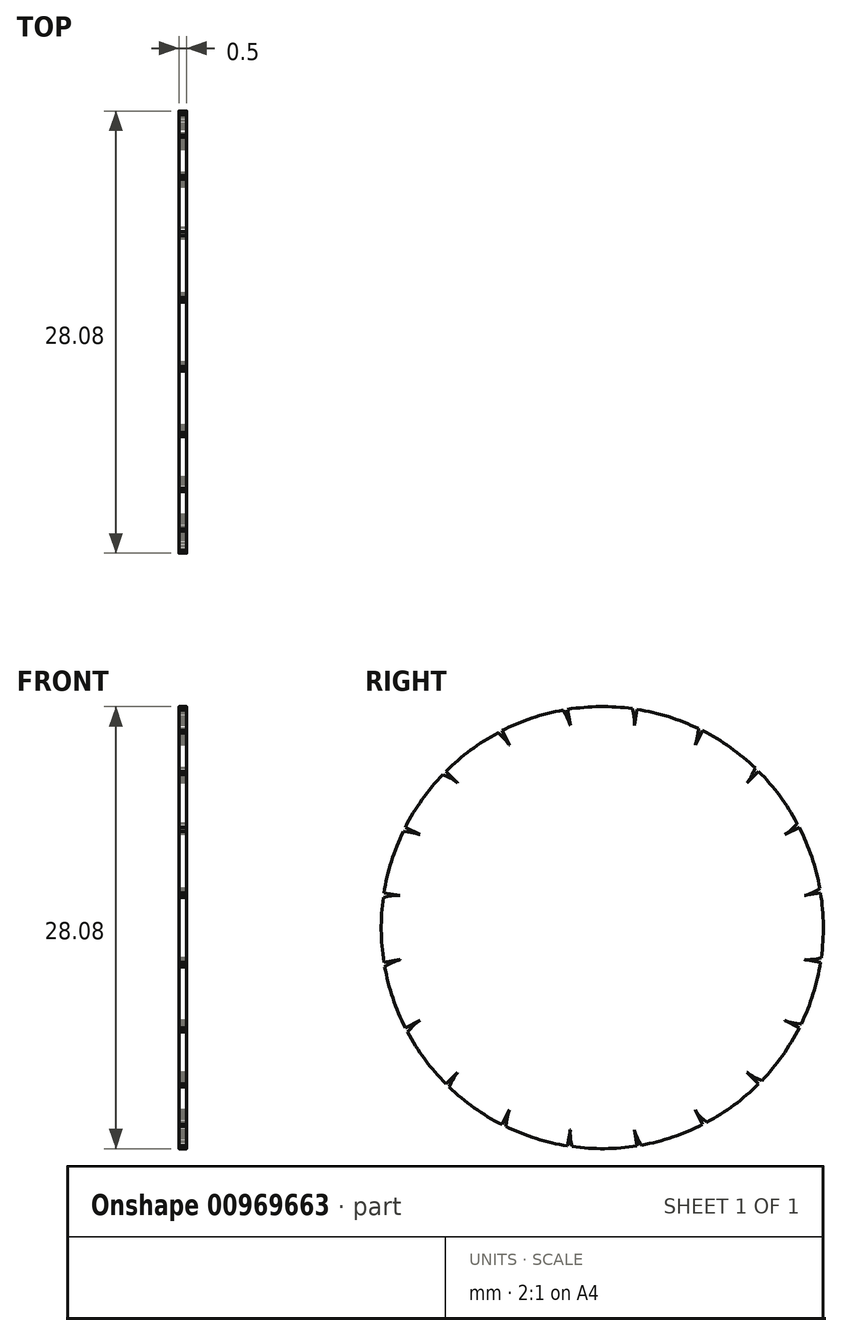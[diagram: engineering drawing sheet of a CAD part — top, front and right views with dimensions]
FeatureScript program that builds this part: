
annotation { "Feature Type Name" : "Feature", "Feature Type Description" : "" }
export const myFeature = defineFeature(function(context is Context, id is Id, definition is map)
    precondition{}
    {
        {
            assignVariable(context, id + "F0", {"name" : "GearThickness", "anyValue" : .5});
        }
        {
            var Q0;
            Q0=qCreatedBy(makeId("Right.planeOp"),FACE);
            var sketch = newSketch(context, id + "F1", { "sketchPlane" : qUnion([Q0])});
            skCircle(sketch, "E0", {"center": v(0, 0) * mm, "radius": 14.04 * mm});
            skCircle(sketch, "E1", {"center": v(0, 0) * mm, "radius": 13 * mm, "construction": true});
            skCircle(sketch, "E2", {"center": v(0, 0) * mm, "radius": 15.88 * mm, "construction": true});
            skCircle(sketch, "E3", {"center": v(0, 0) * mm, "radius": 17.46 * mm});
            skLineSegment(sketch, "E4", {"start": v(0, 0) * mm, "end": v(-13, 0) * mm, "construction": true});
            skLineSegment(sketch, "E5.1.0", {"start": v(0, 0) * mm, "end": v(-12.99, 0.65) * mm, "construction": true});
            skLineSegment(sketch, "E5.2.0", {"start": v(0, 0) * mm, "end": v(-12.94, 1.3) * mm, "construction": true});
            skLineSegment(sketch, "E5.3.0", {"start": v(0, 0) * mm, "end": v(-12.86, 1.94) * mm, "construction": true});
            skLineSegment(sketch, "E5.4.0", {"start": v(0, 0) * mm, "end": v(-12.74, 2.58) * mm, "construction": true});
            skLineSegment(sketch, "E5.5.0", {"start": v(0, 0) * mm, "end": v(-12.6, 3.22) * mm, "construction": true});
            skLineSegment(sketch, "E5.6.0", {"start": v(0, 0) * mm, "end": v(-12.42, 3.84) * mm, "construction": true});
            skLineSegment(sketch, "E5.7.0", {"start": v(0, 0) * mm, "end": v(-12.22, 4.46) * mm, "construction": true});
            skLineSegment(sketch, "E5.8.0", {"start": v(0, 0) * mm, "end": v(-11.98, 5.06) * mm, "construction": true});
            skLineSegment(sketch, "E5.9.0", {"start": v(0, 0) * mm, "end": v(-11.7, 5.66) * mm, "construction": true});
            skLineSegment(sketch, "E5.10.0", {"start": v(0, 0) * mm, "end": v(-11.41, 6.23) * mm, "construction": true});
            skLineSegment(sketch, "E5.11.0", {"start": v(0, 0) * mm, "end": v(-11.09, 6.8) * mm, "construction": true});
            skLineSegment(sketch, "E5.12.0", {"start": v(0, 0) * mm, "end": v(-10.73, 7.34) * mm, "construction": true});
            skLineSegment(sketch, "E5.13.0", {"start": v(0, 0) * mm, "end": v(-10.35, 7.87) * mm, "construction": true});
            skLineSegment(sketch, "E5.14.0", {"start": v(0, 0) * mm, "end": v(-9.95, 8.38) * mm, "construction": true});
            skLineSegment(sketch, "E5.anchor2", {"start": v(0, 0) * mm, "end": v(-9.95, 8.38) * mm, "construction": true});
            skLineSegment(sketch, "E6", {"start": v(-12.99, 0.65) * mm, "end": v(-13.02, 0) * mm, "construction": true});
            skLineSegment(sketch, "E7", {"start": v(-12.94, 1.3) * mm, "end": v(-13.07, 0) * mm, "construction": true});
            skLineSegment(sketch, "E8", {"start": v(-12.86, 1.94) * mm, "end": v(-13.15, 0.01) * mm, "construction": true});
            skLineSegment(sketch, "E9", {"start": v(-12.6, 3.22) * mm, "end": v(-13.4, 0.07) * mm, "construction": true});
            skLineSegment(sketch, "E10", {"start": v(-12.42, 3.84) * mm, "end": v(-13.58, 0.12) * mm, "construction": true});
            skLineSegment(sketch, "E11", {"start": v(-12.22, 4.46) * mm, "end": v(-13.78, 0.18) * mm, "construction": true});
            skLineSegment(sketch, "E12", {"start": v(-11.98, 5.06) * mm, "end": v(-14, 0.27) * mm, "construction": true});
            skLineSegment(sketch, "E13", {"start": v(-11.7, 5.66) * mm, "end": v(-14.25, 0.39) * mm, "construction": true});
            skLineSegment(sketch, "E14", {"start": v(-11.41, 6.23) * mm, "end": v(-14.53, 0.53) * mm, "construction": true});
            skLineSegment(sketch, "E15", {"start": v(-11.09, 6.8) * mm, "end": v(-14.82, 0.7) * mm, "construction": true});
            skLineSegment(sketch, "E16", {"start": v(-12.74, 2.58) * mm, "end": v(-13.26, 0.03) * mm, "construction": true});
            skLineSegment(sketch, "E17", {"start": v(-10.73, 7.34) * mm, "end": v(-15.14, 0.9) * mm, "construction": true});
            skLineSegment(sketch, "E18", {"start": v(-10.35, 7.87) * mm, "end": v(-15.47, 1.14) * mm, "construction": true});
            skLineSegment(sketch, "E19", {"start": v(-9.95, 8.38) * mm, "end": v(-15.81, 1.42) * mm, "construction": true});
            skLineSegment(sketch, "E20", {"start": v(0, 0) * mm, "end": v(-12.96, 1.02) * mm, "construction": true});
            skLineSegment(sketch, "E21", {"start": v(-13, 0) * mm, "end": v(-14.04, 0) * mm});
            skLineSegment(sketch, "E22.MirrorCS", {"start": v(-12.84, 2.03) * mm, "end": v(-13.87, 2.2) * mm});
            skLineSegment(sketch, "E23", {"start": v(-13, 0) * mm, "end": v(-13.02, 0) * mm});
            skLineSegment(sketch, "E24", {"start": v(-13.02, 0) * mm, "end": v(-13.07, 0) * mm});
            skLineSegment(sketch, "E25", {"start": v(-13.07, 0) * mm, "end": v(-13.15, 0.01) * mm});
            skLineSegment(sketch, "E26", {"start": v(-13.15, 0.01) * mm, "end": v(-13.26, 0.03) * mm});
            skLineSegment(sketch, "E27", {"start": v(-13.26, 0.03) * mm, "end": v(-13.4, 0.07) * mm});
            skLineSegment(sketch, "E28", {"start": v(-13.4, 0.07) * mm, "end": v(-13.58, 0.12) * mm});
            skLineSegment(sketch, "E29", {"start": v(-13.58, 0.12) * mm, "end": v(-13.78, 0.18) * mm});
            skLineSegment(sketch, "E30", {"start": v(-13.78, 0.18) * mm, "end": v(-14, 0.27) * mm});
            skLineSegment(sketch, "E31", {"start": v(-14, 0.27) * mm, "end": v(-14.25, 0.39) * mm});
            skLineSegment(sketch, "E32", {"start": v(-14.25, 0.39) * mm, "end": v(-14.53, 0.53) * mm});
            skLineSegment(sketch, "E33", {"start": v(-14.53, 0.53) * mm, "end": v(-14.82, 0.7) * mm});
            skLineSegment(sketch, "E34", {"start": v(-14.82, 0.7) * mm, "end": v(-15.14, 0.9) * mm});
            skLineSegment(sketch, "E35", {"start": v(-15.14, 0.9) * mm, "end": v(-15.47, 1.14) * mm});
            skLineSegment(sketch, "E36", {"start": v(-15.47, 1.14) * mm, "end": v(-15.81, 1.42) * mm});
            skLineSegment(sketch, "E37.MirrorCS", {"start": v(-12.84, 2.03) * mm, "end": v(-12.86, 2.04) * mm});
            skLineSegment(sketch, "E38.MirrorCS", {"start": v(-12.86, 2.04) * mm, "end": v(-12.9, 2.04) * mm});
            skLineSegment(sketch, "E39.MirrorCS", {"start": v(-12.9, 2.04) * mm, "end": v(-12.99, 2.04) * mm});
            skLineSegment(sketch, "E40.MirrorCS", {"start": v(-12.99, 2.04) * mm, "end": v(-13.1, 2.04) * mm});
            skLineSegment(sketch, "E41.MirrorCS", {"start": v(-13.25, 2.03) * mm, "end": v(-13.43, 2) * mm});
            skLineSegment(sketch, "E42.MirrorCS", {"start": v(-13.43, 2) * mm, "end": v(-13.64, 1.97) * mm});
            skLineSegment(sketch, "E43.MirrorCS", {"start": v(-13.64, 1.97) * mm, "end": v(-13.87, 1.92) * mm});
            skLineSegment(sketch, "E44.MirrorCS", {"start": v(-13.87, 1.92) * mm, "end": v(-14.14, 1.85) * mm});
            skLineSegment(sketch, "E45.MirrorCS", {"start": v(-14.43, 1.75) * mm, "end": v(-14.75, 1.63) * mm});
            skLineSegment(sketch, "E46.MirrorCS", {"start": v(-14.14, 1.85) * mm, "end": v(-14.43, 1.75) * mm});
            skLineSegment(sketch, "E47.MirrorCS", {"start": v(-14.75, 1.63) * mm, "end": v(-15.1, 1.48) * mm});
            skLineSegment(sketch, "E48.MirrorCS", {"start": v(-15.1, 1.48) * mm, "end": v(-15.46, 1.3) * mm});
            skLineSegment(sketch, "E49.MirrorCS", {"start": v(-15.46, 1.3) * mm, "end": v(-15.84, 1.08) * mm});
            skLineSegment(sketch, "E50.MirrorCS", {"start": v(-13.1, 2.04) * mm, "end": v(-13.25, 2.03) * mm});
            skLineSegment(sketch, "E51.1.0", {"start": v(-12.37, -4.02) * mm, "end": v(-13.35, -4.34) * mm});
            skLineSegment(sketch, "E51.1.1", {"start": v(-14.53, -3.01) * mm, "end": v(-14.81, -3.26) * mm});
            skLineSegment(sketch, "E51.1.2", {"start": v(-12.84, -2.03) * mm, "end": v(-13.87, -2.2) * mm});
            skLineSegment(sketch, "E51.1.3", {"start": v(-14.27, -2.8) * mm, "end": v(-14.53, -3.01) * mm});
            skLineSegment(sketch, "E51.1.4", {"start": v(-13.98, -3.99) * mm, "end": v(-14.32, -3.92) * mm});
            skLineSegment(sketch, "E51.1.5", {"start": v(-14.32, -3.92) * mm, "end": v(-14.68, -3.82) * mm});
            skLineSegment(sketch, "E51.1.6", {"start": v(-14.02, -2.61) * mm, "end": v(-14.27, -2.8) * mm});
            skLineSegment(sketch, "E51.1.7", {"start": v(-15.1, -3.55) * mm, "end": v(-15.4, -3.87) * mm});
            skLineSegment(sketch, "E51.1.8", {"start": v(-13.79, -2.46) * mm, "end": v(-14.02, -2.61) * mm});
            skLineSegment(sketch, "E51.1.9", {"start": v(-15.06, -3.7) * mm, "end": v(-15.47, -3.54) * mm});
            skLineSegment(sketch, "E51.1.10", {"start": v(-14.81, -3.26) * mm, "end": v(-15.1, -3.55) * mm});
            skLineSegment(sketch, "E51.1.11", {"start": v(-13.68, -4.04) * mm, "end": v(-13.98, -3.99) * mm});
            skLineSegment(sketch, "E51.1.12", {"start": v(-14.68, -3.82) * mm, "end": v(-15.06, -3.7) * mm});
            skLineSegment(sketch, "E51.1.13", {"start": v(-13.23, -2.16) * mm, "end": v(-13.4, -2.24) * mm});
            skLineSegment(sketch, "E51.1.14", {"start": v(-13.4, -2.24) * mm, "end": v(-13.58, -2.34) * mm});
            skLineSegment(sketch, "E51.1.15", {"start": v(-13.58, -2.34) * mm, "end": v(-13.79, -2.46) * mm});
            skLineSegment(sketch, "E51.1.16", {"start": v(-13.16, -4.08) * mm, "end": v(-13.4, -4.07) * mm});
            skLineSegment(sketch, "E51.1.17", {"start": v(-12.95, -4.08) * mm, "end": v(-13.16, -4.08) * mm});
            skLineSegment(sketch, "E51.1.18", {"start": v(-13.4, -4.07) * mm, "end": v(-13.68, -4.04) * mm});
            skLineSegment(sketch, "E51.1.19", {"start": v(-13.1, -2.1) * mm, "end": v(-13.23, -2.16) * mm});
            skLineSegment(sketch, "E51.1.20", {"start": v(-12.99, -2.07) * mm, "end": v(-13.1, -2.1) * mm});
            skLineSegment(sketch, "E51.1.21", {"start": v(-12.77, -4.08) * mm, "end": v(-12.95, -4.08) * mm});
            skLineSegment(sketch, "E51.1.22", {"start": v(-12.62, -4.07) * mm, "end": v(-12.77, -4.08) * mm});
            skLineSegment(sketch, "E51.1.23", {"start": v(-12.43, -4.03) * mm, "end": v(-12.51, -4.05) * mm});
            skLineSegment(sketch, "E51.1.24", {"start": v(-12.84, -2.03) * mm, "end": v(-12.86, -2.04) * mm});
            skLineSegment(sketch, "E51.1.25", {"start": v(-12.86, -2.04) * mm, "end": v(-12.9, -2.05) * mm});
            skLineSegment(sketch, "E51.1.26", {"start": v(-12.51, -4.05) * mm, "end": v(-12.62, -4.07) * mm});
            skLineSegment(sketch, "E51.1.27", {"start": v(-12.9, -2.05) * mm, "end": v(-12.99, -2.07) * mm});
            skLineSegment(sketch, "E51.1.28", {"start": v(-12.38, -4.02) * mm, "end": v(-12.43, -4.03) * mm});
            skLineSegment(sketch, "E51.1.29", {"start": v(-12.37, -4.02) * mm, "end": v(-12.38, -4.02) * mm});
            skLineSegment(sketch, "E51.2.0", {"start": v(-10.52, -7.64) * mm, "end": v(-11.36, -8.25) * mm});
            skLineSegment(sketch, "E51.2.1", {"start": v(-12.9, -7.35) * mm, "end": v(-13.08, -7.68) * mm});
            skLineSegment(sketch, "E51.2.2", {"start": v(-11.59, -5.9) * mm, "end": v(-12.5, -6.37) * mm});
            skLineSegment(sketch, "E51.2.3", {"start": v(-12.7, -7.07) * mm, "end": v(-12.9, -7.35) * mm});
            skLineSegment(sketch, "E51.2.4", {"start": v(-12.07, -8.11) * mm, "end": v(-12.4, -8.15) * mm});
            skLineSegment(sketch, "E51.2.5", {"start": v(-12.4, -8.15) * mm, "end": v(-12.78, -8.17) * mm});
            skLineSegment(sketch, "E51.2.6", {"start": v(-12.53, -6.82) * mm, "end": v(-12.7, -7.07) * mm});
            skLineSegment(sketch, "E51.2.7", {"start": v(-13.26, -8.04) * mm, "end": v(-13.44, -8.44) * mm});
            skLineSegment(sketch, "E51.2.8", {"start": v(-12.35, -6.6) * mm, "end": v(-12.53, -6.82) * mm});
            skLineSegment(sketch, "E51.2.9", {"start": v(-13.18, -8.17) * mm, "end": v(-13.62, -8.15) * mm});
            skLineSegment(sketch, "E51.2.10", {"start": v(-13.08, -7.68) * mm, "end": v(-13.26, -8.04) * mm});
            skLineSegment(sketch, "E51.2.11", {"start": v(-11.76, -8.07) * mm, "end": v(-12.07, -8.11) * mm});
            skLineSegment(sketch, "E51.2.12", {"start": v(-12.78, -8.17) * mm, "end": v(-13.18, -8.17) * mm});
            skLineSegment(sketch, "E51.2.13", {"start": v(-11.91, -6.15) * mm, "end": v(-12.04, -6.27) * mm});
            skLineSegment(sketch, "E51.2.14", {"start": v(-12.04, -6.27) * mm, "end": v(-12.2, -6.42) * mm});
            skLineSegment(sketch, "E51.2.15", {"start": v(-12.2, -6.42) * mm, "end": v(-12.35, -6.6) * mm});
            skLineSegment(sketch, "E51.2.16", {"start": v(-11.25, -7.95) * mm, "end": v(-11.49, -8) * mm});
            skLineSegment(sketch, "E51.2.17", {"start": v(-11.05, -7.89) * mm, "end": v(-11.25, -7.95) * mm});
            skLineSegment(sketch, "E51.2.18", {"start": v(-11.49, -8) * mm, "end": v(-11.76, -8.07) * mm});
            skLineSegment(sketch, "E51.2.19", {"start": v(-11.8, -6.05) * mm, "end": v(-11.91, -6.15) * mm});
            skLineSegment(sketch, "E51.2.20", {"start": v(-11.7, -5.98) * mm, "end": v(-11.8, -6.05) * mm});
            skLineSegment(sketch, "E51.2.21", {"start": v(-10.88, -7.82) * mm, "end": v(-11.05, -7.89) * mm});
            skLineSegment(sketch, "E51.2.22", {"start": v(-10.75, -7.77) * mm, "end": v(-10.88, -7.82) * mm});
            skLineSegment(sketch, "E51.2.23", {"start": v(-10.58, -7.68) * mm, "end": v(-10.65, -7.72) * mm});
            skLineSegment(sketch, "E51.2.24", {"start": v(-11.59, -5.9) * mm, "end": v(-11.6, -5.91) * mm});
            skLineSegment(sketch, "E51.2.25", {"start": v(-11.6, -5.91) * mm, "end": v(-11.64, -5.94) * mm});
            skLineSegment(sketch, "E51.2.26", {"start": v(-10.65, -7.72) * mm, "end": v(-10.75, -7.77) * mm});
            skLineSegment(sketch, "E51.2.27", {"start": v(-11.64, -5.94) * mm, "end": v(-11.7, -5.98) * mm});
            skLineSegment(sketch, "E51.2.28", {"start": v(-10.53, -7.65) * mm, "end": v(-10.58, -7.68) * mm});
            skLineSegment(sketch, "E51.2.29", {"start": v(-10.52, -7.64) * mm, "end": v(-10.53, -7.65) * mm});
            skLineSegment(sketch, "E51.3.0", {"start": v(-7.64, -10.52) * mm, "end": v(-8.25, -11.36) * mm});
            skLineSegment(sketch, "E51.3.1", {"start": v(-9.99, -10.98) * mm, "end": v(-10.07, -11.34) * mm});
            skLineSegment(sketch, "E51.3.2", {"start": v(-9.2, -9.2) * mm, "end": v(-9.93, -9.93) * mm});
            skLineSegment(sketch, "E51.3.3", {"start": v(-9.9, -10.65) * mm, "end": v(-9.99, -10.98) * mm});
            skLineSegment(sketch, "E51.3.4", {"start": v(-8.97, -11.44) * mm, "end": v(-9.28, -11.58) * mm});
            skLineSegment(sketch, "E51.3.5", {"start": v(-9.28, -11.58) * mm, "end": v(-9.63, -11.72) * mm});
            skLineSegment(sketch, "E51.3.6", {"start": v(-9.8, -10.35) * mm, "end": v(-9.9, -10.65) * mm});
            skLineSegment(sketch, "E51.3.7", {"start": v(-10.13, -11.74) * mm, "end": v(-10.18, -12.18) * mm});
            skLineSegment(sketch, "E51.3.8", {"start": v(-9.7, -10.1) * mm, "end": v(-9.8, -10.35) * mm});
            skLineSegment(sketch, "E51.3.9", {"start": v(-10.01, -11.84) * mm, "end": v(-10.44, -11.96) * mm});
            skLineSegment(sketch, "E51.3.10", {"start": v(-10.07, -11.34) * mm, "end": v(-10.13, -11.74) * mm});
            skLineSegment(sketch, "E51.3.11", {"start": v(-8.7, -11.3) * mm, "end": v(-8.97, -11.44) * mm});
            skLineSegment(sketch, "E51.3.12", {"start": v(-9.63, -11.72) * mm, "end": v(-10.01, -11.84) * mm});
            skLineSegment(sketch, "E51.3.13", {"start": v(-9.43, -9.53) * mm, "end": v(-9.52, -9.68) * mm});
            skLineSegment(sketch, "E51.3.14", {"start": v(-9.52, -9.68) * mm, "end": v(-9.61, -9.87) * mm});
            skLineSegment(sketch, "E51.3.15", {"start": v(-9.61, -9.87) * mm, "end": v(-9.7, -10.1) * mm});
            skLineSegment(sketch, "E51.3.16", {"start": v(-8.25, -11.04) * mm, "end": v(-8.45, -11.17) * mm});
            skLineSegment(sketch, "E51.3.17", {"start": v(-8.07, -10.92) * mm, "end": v(-8.25, -11.04) * mm});
            skLineSegment(sketch, "E51.3.18", {"start": v(-8.45, -11.17) * mm, "end": v(-8.7, -11.3) * mm});
            skLineSegment(sketch, "E51.3.19", {"start": v(-9.35, -9.4) * mm, "end": v(-9.43, -9.53) * mm});
            skLineSegment(sketch, "E51.3.20", {"start": v(-9.29, -9.3) * mm, "end": v(-9.35, -9.4) * mm});
            skLineSegment(sketch, "E51.3.21", {"start": v(-7.93, -10.8) * mm, "end": v(-8.07, -10.92) * mm});
            skLineSegment(sketch, "E51.3.22", {"start": v(-7.82, -10.7) * mm, "end": v(-7.93, -10.8) * mm});
            skLineSegment(sketch, "E51.3.23", {"start": v(-7.69, -10.57) * mm, "end": v(-7.74, -10.63) * mm});
            skLineSegment(sketch, "E51.3.24", {"start": v(-9.2, -9.2) * mm, "end": v(-9.2, -9.2) * mm});
            skLineSegment(sketch, "E51.3.25", {"start": v(-9.2, -9.2) * mm, "end": v(-9.24, -9.24) * mm});
            skLineSegment(sketch, "E51.3.26", {"start": v(-7.74, -10.63) * mm, "end": v(-7.82, -10.7) * mm});
            skLineSegment(sketch, "E51.3.27", {"start": v(-9.24, -9.24) * mm, "end": v(-9.29, -9.3) * mm});
            skLineSegment(sketch, "E51.3.28", {"start": v(-7.65, -10.53) * mm, "end": v(-7.69, -10.57) * mm});
            skLineSegment(sketch, "E51.3.29", {"start": v(-7.64, -10.52) * mm, "end": v(-7.65, -10.53) * mm});
            skLineSegment(sketch, "E51.4.0", {"start": v(-4.02, -12.37) * mm, "end": v(-4.34, -13.35) * mm});
            skLineSegment(sketch, "E51.4.1", {"start": v(-6.1, -13.53) * mm, "end": v(-6.07, -13.9) * mm});
            skLineSegment(sketch, "E51.4.2", {"start": v(-5.9, -11.59) * mm, "end": v(-6.37, -12.5) * mm});
            skLineSegment(sketch, "E51.4.3", {"start": v(-6.13, -13.19) * mm, "end": v(-6.1, -13.53) * mm});
            skLineSegment(sketch, "E51.4.4", {"start": v(-5, -13.65) * mm, "end": v(-5.25, -13.88) * mm});
            skLineSegment(sketch, "E51.4.5", {"start": v(-5.25, -13.88) * mm, "end": v(-5.54, -14.12) * mm});
            skLineSegment(sketch, "E51.4.6", {"start": v(-6.13, -12.88) * mm, "end": v(-6.13, -13.19) * mm});
            skLineSegment(sketch, "E51.4.7", {"start": v(-6, -14.3) * mm, "end": v(-5.92, -14.73) * mm});
            skLineSegment(sketch, "E51.4.8", {"start": v(-6.11, -12.6) * mm, "end": v(-6.13, -12.88) * mm});
            skLineSegment(sketch, "E51.4.9", {"start": v(-5.86, -14.36) * mm, "end": v(-6.23, -14.6) * mm});
            skLineSegment(sketch, "E51.4.10", {"start": v(-6.07, -13.9) * mm, "end": v(-6, -14.3) * mm});
            skLineSegment(sketch, "E51.4.11", {"start": v(-4.77, -13.44) * mm, "end": v(-5, -13.65) * mm});
            skLineSegment(sketch, "E51.4.12", {"start": v(-5.54, -14.12) * mm, "end": v(-5.86, -14.36) * mm});
            skLineSegment(sketch, "E51.4.13", {"start": v(-6.03, -11.97) * mm, "end": v(-6.06, -12.15) * mm});
            skLineSegment(sketch, "E51.4.14", {"start": v(-6.06, -12.15) * mm, "end": v(-6.1, -12.36) * mm});
            skLineSegment(sketch, "E51.4.15", {"start": v(-6.1, -12.36) * mm, "end": v(-6.11, -12.6) * mm});
            skLineSegment(sketch, "E51.4.16", {"start": v(-4.43, -13.05) * mm, "end": v(-4.59, -13.23) * mm});
            skLineSegment(sketch, "E51.4.17", {"start": v(-4.3, -12.88) * mm, "end": v(-4.43, -13.05) * mm});
            skLineSegment(sketch, "E51.4.18", {"start": v(-4.59, -13.23) * mm, "end": v(-4.77, -13.44) * mm});
            skLineSegment(sketch, "E51.4.19", {"start": v(-5.99, -11.83) * mm, "end": v(-6.03, -11.97) * mm});
            skLineSegment(sketch, "E51.4.20", {"start": v(-5.96, -11.72) * mm, "end": v(-5.99, -11.83) * mm});
            skLineSegment(sketch, "E51.4.21", {"start": v(-4.2, -12.73) * mm, "end": v(-4.3, -12.88) * mm});
            skLineSegment(sketch, "E51.4.22", {"start": v(-4.13, -12.6) * mm, "end": v(-4.2, -12.73) * mm});
            skLineSegment(sketch, "E51.4.23", {"start": v(-4.04, -12.43) * mm, "end": v(-4.08, -12.5) * mm});
            skLineSegment(sketch, "E51.4.24", {"start": v(-5.9, -11.59) * mm, "end": v(-5.91, -11.6) * mm});
            skLineSegment(sketch, "E51.4.25", {"start": v(-5.91, -11.6) * mm, "end": v(-5.93, -11.65) * mm});
            skLineSegment(sketch, "E51.4.26", {"start": v(-4.08, -12.5) * mm, "end": v(-4.13, -12.6) * mm});
            skLineSegment(sketch, "E51.4.27", {"start": v(-5.93, -11.65) * mm, "end": v(-5.96, -11.72) * mm});
            skLineSegment(sketch, "E51.4.28", {"start": v(-4.02, -12.38) * mm, "end": v(-4.04, -12.43) * mm});
            skLineSegment(sketch, "E51.4.29", {"start": v(-4.02, -12.37) * mm, "end": v(-4.02, -12.38) * mm});
            skLineSegment(sketch, "E51.5.0", {"start": v(0, -13) * mm, "end": v(0, -14.04) * mm});
            skLineSegment(sketch, "E51.5.1", {"start": v(-1.63, -14.75) * mm, "end": v(-1.48, -15.1) * mm});
            skLineSegment(sketch, "E51.5.2", {"start": v(-2.03, -12.84) * mm, "end": v(-2.2, -13.87) * mm});
            skLineSegment(sketch, "E51.5.3", {"start": v(-1.75, -14.43) * mm, "end": v(-1.63, -14.75) * mm});
            skLineSegment(sketch, "E51.5.4", {"start": v(-0.53, -14.53) * mm, "end": v(-0.7, -14.82) * mm});
            skLineSegment(sketch, "E51.5.5", {"start": v(-0.7, -14.82) * mm, "end": v(-0.9, -15.14) * mm});
            skLineSegment(sketch, "E51.5.6", {"start": v(-1.85, -14.14) * mm, "end": v(-1.75, -14.43) * mm});
            skLineSegment(sketch, "E51.5.7", {"start": v(-1.3, -15.46) * mm, "end": v(-1.08, -15.84) * mm});
            skLineSegment(sketch, "E51.5.8", {"start": v(-1.92, -13.87) * mm, "end": v(-1.85, -14.14) * mm});
            skLineSegment(sketch, "E51.5.9", {"start": v(-1.14, -15.47) * mm, "end": v(-1.42, -15.81) * mm});
            skLineSegment(sketch, "E51.5.10", {"start": v(-1.48, -15.1) * mm, "end": v(-1.3, -15.46) * mm});
            skLineSegment(sketch, "E51.5.11", {"start": v(-0.39, -14.25) * mm, "end": v(-0.53, -14.53) * mm});
            skLineSegment(sketch, "E51.5.12", {"start": v(-0.9, -15.14) * mm, "end": v(-1.14, -15.47) * mm});
            skLineSegment(sketch, "E51.5.13", {"start": v(-2.03, -13.25) * mm, "end": v(-2, -13.43) * mm});
            skLineSegment(sketch, "E51.5.14", {"start": v(-2, -13.43) * mm, "end": v(-1.97, -13.64) * mm});
            skLineSegment(sketch, "E51.5.15", {"start": v(-1.97, -13.64) * mm, "end": v(-1.92, -13.87) * mm});
            skLineSegment(sketch, "E51.5.16", {"start": v(-0.18, -13.78) * mm, "end": v(-0.27, -14) * mm});
            skLineSegment(sketch, "E51.5.17", {"start": v(-0.12, -13.58) * mm, "end": v(-0.18, -13.78) * mm});
            skLineSegment(sketch, "E51.5.18", {"start": v(-0.27, -14) * mm, "end": v(-0.39, -14.25) * mm});
            skLineSegment(sketch, "E51.5.19", {"start": v(-2.04, -13.1) * mm, "end": v(-2.03, -13.25) * mm});
            skLineSegment(sketch, "E51.5.20", {"start": v(-2.04, -12.99) * mm, "end": v(-2.04, -13.1) * mm});
            skLineSegment(sketch, "E51.5.21", {"start": v(-0.07, -13.4) * mm, "end": v(-0.12, -13.58) * mm});
            skLineSegment(sketch, "E51.5.22", {"start": v(-0.03, -13.26) * mm, "end": v(-0.07, -13.4) * mm});
            skLineSegment(sketch, "E51.5.23", {"start": v(0, -13.07) * mm, "end": v(-0.01, -13.15) * mm});
            skLineSegment(sketch, "E51.5.24", {"start": v(-2.03, -12.84) * mm, "end": v(-2.04, -12.86) * mm});
            skLineSegment(sketch, "E51.5.25", {"start": v(-2.04, -12.86) * mm, "end": v(-2.04, -12.9) * mm});
            skLineSegment(sketch, "E51.5.26", {"start": v(-0.01, -13.15) * mm, "end": v(-0.03, -13.26) * mm});
            skLineSegment(sketch, "E51.5.27", {"start": v(-2.04, -12.9) * mm, "end": v(-2.04, -12.99) * mm});
            skLineSegment(sketch, "E51.5.28", {"start": v(0, -13.02) * mm, "end": v(0, -13.07) * mm});
            skLineSegment(sketch, "E51.5.29", {"start": v(0, -13) * mm, "end": v(0, -13.02) * mm});
            skLineSegment(sketch, "E51.6.0", {"start": v(4.02, -12.37) * mm, "end": v(4.34, -13.35) * mm});
            skLineSegment(sketch, "E51.6.1", {"start": v(3.01, -14.53) * mm, "end": v(3.26, -14.81) * mm});
            skLineSegment(sketch, "E51.6.2", {"start": v(2.03, -12.84) * mm, "end": v(2.2, -13.87) * mm});
            skLineSegment(sketch, "E51.6.3", {"start": v(2.8, -14.27) * mm, "end": v(3.01, -14.53) * mm});
            skLineSegment(sketch, "E51.6.4", {"start": v(3.99, -13.98) * mm, "end": v(3.92, -14.32) * mm});
            skLineSegment(sketch, "E51.6.5", {"start": v(3.92, -14.32) * mm, "end": v(3.82, -14.68) * mm});
            skLineSegment(sketch, "E51.6.6", {"start": v(2.61, -14.02) * mm, "end": v(2.8, -14.27) * mm});
            skLineSegment(sketch, "E51.6.7", {"start": v(3.55, -15.1) * mm, "end": v(3.87, -15.4) * mm});
            skLineSegment(sketch, "E51.6.8", {"start": v(2.46, -13.79) * mm, "end": v(2.61, -14.02) * mm});
            skLineSegment(sketch, "E51.6.9", {"start": v(3.7, -15.06) * mm, "end": v(3.54, -15.47) * mm});
            skLineSegment(sketch, "E51.6.10", {"start": v(3.26, -14.81) * mm, "end": v(3.55, -15.1) * mm});
            skLineSegment(sketch, "E51.6.11", {"start": v(4.04, -13.68) * mm, "end": v(3.99, -13.98) * mm});
            skLineSegment(sketch, "E51.6.12", {"start": v(3.82, -14.68) * mm, "end": v(3.7, -15.06) * mm});
            skLineSegment(sketch, "E51.6.13", {"start": v(2.16, -13.23) * mm, "end": v(2.24, -13.4) * mm});
            skLineSegment(sketch, "E51.6.14", {"start": v(2.24, -13.4) * mm, "end": v(2.34, -13.58) * mm});
            skLineSegment(sketch, "E51.6.15", {"start": v(2.34, -13.58) * mm, "end": v(2.46, -13.79) * mm});
            skLineSegment(sketch, "E51.6.16", {"start": v(4.08, -13.16) * mm, "end": v(4.07, -13.4) * mm});
            skLineSegment(sketch, "E51.6.17", {"start": v(4.08, -12.95) * mm, "end": v(4.08, -13.16) * mm});
            skLineSegment(sketch, "E51.6.18", {"start": v(4.07, -13.4) * mm, "end": v(4.04, -13.68) * mm});
            skLineSegment(sketch, "E51.6.19", {"start": v(2.1, -13.1) * mm, "end": v(2.16, -13.23) * mm});
            skLineSegment(sketch, "E51.6.20", {"start": v(2.07, -12.99) * mm, "end": v(2.1, -13.1) * mm});
            skLineSegment(sketch, "E51.6.21", {"start": v(4.08, -12.77) * mm, "end": v(4.08, -12.95) * mm});
            skLineSegment(sketch, "E51.6.22", {"start": v(4.07, -12.62) * mm, "end": v(4.08, -12.77) * mm});
            skLineSegment(sketch, "E51.6.23", {"start": v(4.03, -12.43) * mm, "end": v(4.05, -12.51) * mm});
            skLineSegment(sketch, "E51.6.24", {"start": v(2.03, -12.84) * mm, "end": v(2.04, -12.86) * mm});
            skLineSegment(sketch, "E51.6.25", {"start": v(2.04, -12.86) * mm, "end": v(2.05, -12.9) * mm});
            skLineSegment(sketch, "E51.6.26", {"start": v(4.05, -12.51) * mm, "end": v(4.07, -12.62) * mm});
            skLineSegment(sketch, "E51.6.27", {"start": v(2.05, -12.9) * mm, "end": v(2.07, -12.99) * mm});
            skLineSegment(sketch, "E51.6.28", {"start": v(4.02, -12.38) * mm, "end": v(4.03, -12.43) * mm});
            skLineSegment(sketch, "E51.6.29", {"start": v(4.02, -12.37) * mm, "end": v(4.02, -12.38) * mm});
            skLineSegment(sketch, "E51.7.0", {"start": v(7.64, -10.52) * mm, "end": v(8.25, -11.36) * mm});
            skLineSegment(sketch, "E51.7.1", {"start": v(7.35, -12.9) * mm, "end": v(7.68, -13.08) * mm});
            skLineSegment(sketch, "E51.7.2", {"start": v(5.9, -11.59) * mm, "end": v(6.37, -12.5) * mm});
            skLineSegment(sketch, "E51.7.3", {"start": v(7.07, -12.7) * mm, "end": v(7.35, -12.9) * mm});
            skLineSegment(sketch, "E51.7.4", {"start": v(8.11, -12.07) * mm, "end": v(8.15, -12.4) * mm});
            skLineSegment(sketch, "E51.7.5", {"start": v(8.15, -12.4) * mm, "end": v(8.17, -12.78) * mm});
            skLineSegment(sketch, "E51.7.6", {"start": v(6.82, -12.53) * mm, "end": v(7.07, -12.7) * mm});
            skLineSegment(sketch, "E51.7.7", {"start": v(8.04, -13.26) * mm, "end": v(8.44, -13.44) * mm});
            skLineSegment(sketch, "E51.7.8", {"start": v(6.6, -12.35) * mm, "end": v(6.82, -12.53) * mm});
            skLineSegment(sketch, "E51.7.9", {"start": v(8.17, -13.18) * mm, "end": v(8.15, -13.62) * mm});
            skLineSegment(sketch, "E51.7.10", {"start": v(7.68, -13.08) * mm, "end": v(8.04, -13.26) * mm});
            skLineSegment(sketch, "E51.7.11", {"start": v(8.07, -11.76) * mm, "end": v(8.11, -12.07) * mm});
            skLineSegment(sketch, "E51.7.12", {"start": v(8.17, -12.78) * mm, "end": v(8.17, -13.18) * mm});
            skLineSegment(sketch, "E51.7.13", {"start": v(6.15, -11.91) * mm, "end": v(6.27, -12.04) * mm});
            skLineSegment(sketch, "E51.7.14", {"start": v(6.27, -12.04) * mm, "end": v(6.42, -12.2) * mm});
            skLineSegment(sketch, "E51.7.15", {"start": v(6.42, -12.2) * mm, "end": v(6.6, -12.35) * mm});
            skLineSegment(sketch, "E51.7.16", {"start": v(7.95, -11.25) * mm, "end": v(8, -11.49) * mm});
            skLineSegment(sketch, "E51.7.17", {"start": v(7.89, -11.05) * mm, "end": v(7.95, -11.25) * mm});
            skLineSegment(sketch, "E51.7.18", {"start": v(8, -11.49) * mm, "end": v(8.07, -11.76) * mm});
            skLineSegment(sketch, "E51.7.19", {"start": v(6.05, -11.8) * mm, "end": v(6.15, -11.91) * mm});
            skLineSegment(sketch, "E51.7.20", {"start": v(5.98, -11.7) * mm, "end": v(6.05, -11.8) * mm});
            skLineSegment(sketch, "E51.7.21", {"start": v(7.82, -10.88) * mm, "end": v(7.89, -11.05) * mm});
            skLineSegment(sketch, "E51.7.22", {"start": v(7.77, -10.75) * mm, "end": v(7.82, -10.88) * mm});
            skLineSegment(sketch, "E51.7.23", {"start": v(7.68, -10.58) * mm, "end": v(7.72, -10.65) * mm});
            skLineSegment(sketch, "E51.7.24", {"start": v(5.9, -11.59) * mm, "end": v(5.91, -11.6) * mm});
            skLineSegment(sketch, "E51.7.25", {"start": v(5.91, -11.6) * mm, "end": v(5.94, -11.64) * mm});
            skLineSegment(sketch, "E51.7.26", {"start": v(7.72, -10.65) * mm, "end": v(7.77, -10.75) * mm});
            skLineSegment(sketch, "E51.7.27", {"start": v(5.94, -11.64) * mm, "end": v(5.98, -11.7) * mm});
            skLineSegment(sketch, "E51.7.28", {"start": v(7.65, -10.53) * mm, "end": v(7.68, -10.58) * mm});
            skLineSegment(sketch, "E51.7.29", {"start": v(7.64, -10.52) * mm, "end": v(7.65, -10.53) * mm});
            skLineSegment(sketch, "E51.8.0", {"start": v(10.52, -7.64) * mm, "end": v(11.36, -8.25) * mm});
            skLineSegment(sketch, "E51.8.1", {"start": v(10.98, -9.99) * mm, "end": v(11.34, -10.07) * mm});
            skLineSegment(sketch, "E51.8.2", {"start": v(9.2, -9.2) * mm, "end": v(9.93, -9.93) * mm});
            skLineSegment(sketch, "E51.8.3", {"start": v(10.65, -9.9) * mm, "end": v(10.98, -9.99) * mm});
            skLineSegment(sketch, "E51.8.4", {"start": v(11.44, -8.97) * mm, "end": v(11.58, -9.28) * mm});
            skLineSegment(sketch, "E51.8.5", {"start": v(11.58, -9.28) * mm, "end": v(11.72, -9.63) * mm});
            skLineSegment(sketch, "E51.8.6", {"start": v(10.35, -9.8) * mm, "end": v(10.65, -9.9) * mm});
            skLineSegment(sketch, "E51.8.7", {"start": v(11.74, -10.13) * mm, "end": v(12.18, -10.18) * mm});
            skLineSegment(sketch, "E51.8.8", {"start": v(10.1, -9.7) * mm, "end": v(10.35, -9.8) * mm});
            skLineSegment(sketch, "E51.8.9", {"start": v(11.84, -10.01) * mm, "end": v(11.96, -10.44) * mm});
            skLineSegment(sketch, "E51.8.10", {"start": v(11.34, -10.07) * mm, "end": v(11.74, -10.13) * mm});
            skLineSegment(sketch, "E51.8.11", {"start": v(11.3, -8.7) * mm, "end": v(11.44, -8.97) * mm});
            skLineSegment(sketch, "E51.8.12", {"start": v(11.72, -9.63) * mm, "end": v(11.84, -10.01) * mm});
            skLineSegment(sketch, "E51.8.13", {"start": v(9.53, -9.43) * mm, "end": v(9.68, -9.52) * mm});
            skLineSegment(sketch, "E51.8.14", {"start": v(9.68, -9.52) * mm, "end": v(9.87, -9.61) * mm});
            skLineSegment(sketch, "E51.8.15", {"start": v(9.87, -9.61) * mm, "end": v(10.1, -9.7) * mm});
            skLineSegment(sketch, "E51.8.16", {"start": v(11.04, -8.25) * mm, "end": v(11.17, -8.45) * mm});
            skLineSegment(sketch, "E51.8.17", {"start": v(10.92, -8.07) * mm, "end": v(11.04, -8.25) * mm});
            skLineSegment(sketch, "E51.8.18", {"start": v(11.17, -8.45) * mm, "end": v(11.3, -8.7) * mm});
            skLineSegment(sketch, "E51.8.19", {"start": v(9.4, -9.35) * mm, "end": v(9.53, -9.43) * mm});
            skLineSegment(sketch, "E51.8.20", {"start": v(9.3, -9.29) * mm, "end": v(9.4, -9.35) * mm});
            skLineSegment(sketch, "E51.8.21", {"start": v(10.8, -7.93) * mm, "end": v(10.92, -8.07) * mm});
            skLineSegment(sketch, "E51.8.22", {"start": v(10.7, -7.82) * mm, "end": v(10.8, -7.93) * mm});
            skLineSegment(sketch, "E51.8.23", {"start": v(10.57, -7.69) * mm, "end": v(10.63, -7.74) * mm});
            skLineSegment(sketch, "E51.8.24", {"start": v(9.2, -9.2) * mm, "end": v(9.2, -9.2) * mm});
            skLineSegment(sketch, "E51.8.25", {"start": v(9.2, -9.2) * mm, "end": v(9.24, -9.24) * mm});
            skLineSegment(sketch, "E51.8.26", {"start": v(10.63, -7.74) * mm, "end": v(10.7, -7.82) * mm});
            skLineSegment(sketch, "E51.8.27", {"start": v(9.24, -9.24) * mm, "end": v(9.3, -9.29) * mm});
            skLineSegment(sketch, "E51.8.28", {"start": v(10.53, -7.65) * mm, "end": v(10.57, -7.69) * mm});
            skLineSegment(sketch, "E51.8.29", {"start": v(10.52, -7.64) * mm, "end": v(10.53, -7.65) * mm});
            skLineSegment(sketch, "E51.9.0", {"start": v(12.37, -4.02) * mm, "end": v(13.35, -4.34) * mm});
            skLineSegment(sketch, "E51.9.1", {"start": v(13.53, -6.1) * mm, "end": v(13.9, -6.07) * mm});
            skLineSegment(sketch, "E51.9.2", {"start": v(11.59, -5.9) * mm, "end": v(12.5, -6.37) * mm});
            skLineSegment(sketch, "E51.9.3", {"start": v(13.19, -6.13) * mm, "end": v(13.53, -6.1) * mm});
            skLineSegment(sketch, "E51.9.4", {"start": v(13.65, -5) * mm, "end": v(13.88, -5.25) * mm});
            skLineSegment(sketch, "E51.9.5", {"start": v(13.88, -5.25) * mm, "end": v(14.12, -5.54) * mm});
            skLineSegment(sketch, "E51.9.6", {"start": v(12.88, -6.13) * mm, "end": v(13.19, -6.13) * mm});
            skLineSegment(sketch, "E51.9.7", {"start": v(14.3, -6) * mm, "end": v(14.73, -5.92) * mm});
            skLineSegment(sketch, "E51.9.8", {"start": v(12.6, -6.11) * mm, "end": v(12.88, -6.13) * mm});
            skLineSegment(sketch, "E51.9.9", {"start": v(14.36, -5.86) * mm, "end": v(14.6, -6.23) * mm});
            skLineSegment(sketch, "E51.9.10", {"start": v(13.9, -6.07) * mm, "end": v(14.3, -6) * mm});
            skLineSegment(sketch, "E51.9.11", {"start": v(13.44, -4.77) * mm, "end": v(13.65, -5) * mm});
            skLineSegment(sketch, "E51.9.12", {"start": v(14.12, -5.54) * mm, "end": v(14.36, -5.86) * mm});
            skLineSegment(sketch, "E51.9.13", {"start": v(11.97, -6.03) * mm, "end": v(12.15, -6.06) * mm});
            skLineSegment(sketch, "E51.9.14", {"start": v(12.15, -6.06) * mm, "end": v(12.36, -6.1) * mm});
            skLineSegment(sketch, "E51.9.15", {"start": v(12.36, -6.1) * mm, "end": v(12.6, -6.11) * mm});
            skLineSegment(sketch, "E51.9.16", {"start": v(13.05, -4.43) * mm, "end": v(13.23, -4.59) * mm});
            skLineSegment(sketch, "E51.9.17", {"start": v(12.88, -4.3) * mm, "end": v(13.05, -4.43) * mm});
            skLineSegment(sketch, "E51.9.18", {"start": v(13.23, -4.59) * mm, "end": v(13.44, -4.77) * mm});
            skLineSegment(sketch, "E51.9.19", {"start": v(11.83, -5.99) * mm, "end": v(11.97, -6.03) * mm});
            skLineSegment(sketch, "E51.9.20", {"start": v(11.72, -5.96) * mm, "end": v(11.83, -5.99) * mm});
            skLineSegment(sketch, "E51.9.21", {"start": v(12.73, -4.2) * mm, "end": v(12.88, -4.3) * mm});
            skLineSegment(sketch, "E51.9.22", {"start": v(12.6, -4.13) * mm, "end": v(12.73, -4.2) * mm});
            skLineSegment(sketch, "E51.9.23", {"start": v(12.43, -4.04) * mm, "end": v(12.5, -4.08) * mm});
            skLineSegment(sketch, "E51.9.24", {"start": v(11.59, -5.9) * mm, "end": v(11.6, -5.91) * mm});
            skLineSegment(sketch, "E51.9.25", {"start": v(11.6, -5.91) * mm, "end": v(11.65, -5.93) * mm});
            skLineSegment(sketch, "E51.9.26", {"start": v(12.5, -4.08) * mm, "end": v(12.6, -4.13) * mm});
            skLineSegment(sketch, "E51.9.27", {"start": v(11.65, -5.93) * mm, "end": v(11.72, -5.96) * mm});
            skLineSegment(sketch, "E51.9.28", {"start": v(12.38, -4.02) * mm, "end": v(12.43, -4.04) * mm});
            skLineSegment(sketch, "E51.9.29", {"start": v(12.37, -4.02) * mm, "end": v(12.38, -4.02) * mm});
            skLineSegment(sketch, "E51.10.0", {"start": v(13, 0) * mm, "end": v(14.04, 0) * mm});
            skLineSegment(sketch, "E51.10.1", {"start": v(14.75, -1.63) * mm, "end": v(15.1, -1.48) * mm});
            skLineSegment(sketch, "E51.10.2", {"start": v(12.84, -2.03) * mm, "end": v(13.87, -2.2) * mm});
            skLineSegment(sketch, "E51.10.3", {"start": v(14.43, -1.75) * mm, "end": v(14.75, -1.63) * mm});
            skLineSegment(sketch, "E51.10.4", {"start": v(14.53, -0.53) * mm, "end": v(14.82, -0.7) * mm});
            skLineSegment(sketch, "E51.10.5", {"start": v(14.82, -0.7) * mm, "end": v(15.14, -0.9) * mm});
            skLineSegment(sketch, "E51.10.6", {"start": v(14.14, -1.85) * mm, "end": v(14.43, -1.75) * mm});
            skLineSegment(sketch, "E51.10.7", {"start": v(15.46, -1.3) * mm, "end": v(15.84, -1.08) * mm});
            skLineSegment(sketch, "E51.10.8", {"start": v(13.87, -1.92) * mm, "end": v(14.14, -1.85) * mm});
            skLineSegment(sketch, "E51.10.9", {"start": v(15.47, -1.14) * mm, "end": v(15.81, -1.42) * mm});
            skLineSegment(sketch, "E51.10.10", {"start": v(15.1, -1.48) * mm, "end": v(15.46, -1.3) * mm});
            skLineSegment(sketch, "E51.10.11", {"start": v(14.25, -0.39) * mm, "end": v(14.53, -0.53) * mm});
            skLineSegment(sketch, "E51.10.12", {"start": v(15.14, -0.9) * mm, "end": v(15.47, -1.14) * mm});
            skLineSegment(sketch, "E51.10.13", {"start": v(13.25, -2.03) * mm, "end": v(13.43, -2) * mm});
            skLineSegment(sketch, "E51.10.14", {"start": v(13.43, -2) * mm, "end": v(13.64, -1.97) * mm});
            skLineSegment(sketch, "E51.10.15", {"start": v(13.64, -1.97) * mm, "end": v(13.87, -1.92) * mm});
            skLineSegment(sketch, "E51.10.16", {"start": v(13.78, -0.18) * mm, "end": v(14, -0.27) * mm});
            skLineSegment(sketch, "E51.10.17", {"start": v(13.58, -0.12) * mm, "end": v(13.78, -0.18) * mm});
            skLineSegment(sketch, "E51.10.18", {"start": v(14, -0.27) * mm, "end": v(14.25, -0.39) * mm});
            skLineSegment(sketch, "E51.10.19", {"start": v(13.1, -2.04) * mm, "end": v(13.25, -2.03) * mm});
            skLineSegment(sketch, "E51.10.20", {"start": v(12.99, -2.04) * mm, "end": v(13.1, -2.04) * mm});
            skLineSegment(sketch, "E51.10.21", {"start": v(13.4, -0.07) * mm, "end": v(13.58, -0.12) * mm});
            skLineSegment(sketch, "E51.10.22", {"start": v(13.26, -0.03) * mm, "end": v(13.4, -0.07) * mm});
            skLineSegment(sketch, "E51.10.23", {"start": v(13.07, 0) * mm, "end": v(13.15, -0.01) * mm});
            skLineSegment(sketch, "E51.10.24", {"start": v(12.84, -2.03) * mm, "end": v(12.86, -2.04) * mm});
            skLineSegment(sketch, "E51.10.25", {"start": v(12.86, -2.04) * mm, "end": v(12.9, -2.04) * mm});
            skLineSegment(sketch, "E51.10.26", {"start": v(13.15, -0.01) * mm, "end": v(13.26, -0.03) * mm});
            skLineSegment(sketch, "E51.10.27", {"start": v(12.9, -2.04) * mm, "end": v(12.99, -2.04) * mm});
            skLineSegment(sketch, "E51.10.28", {"start": v(13.02, 0) * mm, "end": v(13.07, 0) * mm});
            skLineSegment(sketch, "E51.10.29", {"start": v(13, 0) * mm, "end": v(13.02, 0) * mm});
            skLineSegment(sketch, "E51.11.0", {"start": v(12.37, 4.02) * mm, "end": v(13.35, 4.34) * mm});
            skLineSegment(sketch, "E51.11.1", {"start": v(14.53, 3.01) * mm, "end": v(14.81, 3.26) * mm});
            skLineSegment(sketch, "E51.11.2", {"start": v(12.84, 2.03) * mm, "end": v(13.87, 2.2) * mm});
            skLineSegment(sketch, "E51.11.3", {"start": v(14.27, 2.8) * mm, "end": v(14.53, 3.01) * mm});
            skLineSegment(sketch, "E51.11.4", {"start": v(13.98, 3.99) * mm, "end": v(14.32, 3.92) * mm});
            skLineSegment(sketch, "E51.11.5", {"start": v(14.32, 3.92) * mm, "end": v(14.68, 3.82) * mm});
            skLineSegment(sketch, "E51.11.6", {"start": v(14.02, 2.61) * mm, "end": v(14.27, 2.8) * mm});
            skLineSegment(sketch, "E51.11.7", {"start": v(15.1, 3.55) * mm, "end": v(15.4, 3.87) * mm});
            skLineSegment(sketch, "E51.11.8", {"start": v(13.79, 2.46) * mm, "end": v(14.02, 2.61) * mm});
            skLineSegment(sketch, "E51.11.9", {"start": v(15.06, 3.7) * mm, "end": v(15.47, 3.54) * mm});
            skLineSegment(sketch, "E51.11.10", {"start": v(14.81, 3.26) * mm, "end": v(15.1, 3.55) * mm});
            skLineSegment(sketch, "E51.11.11", {"start": v(13.68, 4.04) * mm, "end": v(13.98, 3.99) * mm});
            skLineSegment(sketch, "E51.11.12", {"start": v(14.68, 3.82) * mm, "end": v(15.06, 3.7) * mm});
            skLineSegment(sketch, "E51.11.13", {"start": v(13.23, 2.16) * mm, "end": v(13.4, 2.24) * mm});
            skLineSegment(sketch, "E51.11.14", {"start": v(13.4, 2.24) * mm, "end": v(13.58, 2.34) * mm});
            skLineSegment(sketch, "E51.11.15", {"start": v(13.58, 2.34) * mm, "end": v(13.79, 2.46) * mm});
            skLineSegment(sketch, "E51.11.16", {"start": v(13.16, 4.08) * mm, "end": v(13.4, 4.07) * mm});
            skLineSegment(sketch, "E51.11.17", {"start": v(12.95, 4.08) * mm, "end": v(13.16, 4.08) * mm});
            skLineSegment(sketch, "E51.11.18", {"start": v(13.4, 4.07) * mm, "end": v(13.68, 4.04) * mm});
            skLineSegment(sketch, "E51.11.19", {"start": v(13.1, 2.1) * mm, "end": v(13.23, 2.16) * mm});
            skLineSegment(sketch, "E51.11.20", {"start": v(12.99, 2.07) * mm, "end": v(13.1, 2.1) * mm});
            skLineSegment(sketch, "E51.11.21", {"start": v(12.77, 4.08) * mm, "end": v(12.95, 4.08) * mm});
            skLineSegment(sketch, "E51.11.22", {"start": v(12.62, 4.07) * mm, "end": v(12.77, 4.08) * mm});
            skLineSegment(sketch, "E51.11.23", {"start": v(12.43, 4.03) * mm, "end": v(12.51, 4.05) * mm});
            skLineSegment(sketch, "E51.11.24", {"start": v(12.84, 2.03) * mm, "end": v(12.86, 2.04) * mm});
            skLineSegment(sketch, "E51.11.25", {"start": v(12.86, 2.04) * mm, "end": v(12.9, 2.05) * mm});
            skLineSegment(sketch, "E51.11.26", {"start": v(12.51, 4.05) * mm, "end": v(12.62, 4.07) * mm});
            skLineSegment(sketch, "E51.11.27", {"start": v(12.9, 2.05) * mm, "end": v(12.99, 2.07) * mm});
            skLineSegment(sketch, "E51.11.28", {"start": v(12.38, 4.02) * mm, "end": v(12.43, 4.03) * mm});
            skLineSegment(sketch, "E51.11.29", {"start": v(12.37, 4.02) * mm, "end": v(12.38, 4.02) * mm});
            skLineSegment(sketch, "E51.12.0", {"start": v(10.52, 7.64) * mm, "end": v(11.36, 8.25) * mm});
            skLineSegment(sketch, "E51.12.1", {"start": v(12.9, 7.35) * mm, "end": v(13.08, 7.68) * mm});
            skLineSegment(sketch, "E51.12.2", {"start": v(11.59, 5.9) * mm, "end": v(12.5, 6.37) * mm});
            skLineSegment(sketch, "E51.12.3", {"start": v(12.7, 7.07) * mm, "end": v(12.9, 7.35) * mm});
            skLineSegment(sketch, "E51.12.4", {"start": v(12.07, 8.11) * mm, "end": v(12.4, 8.15) * mm});
            skLineSegment(sketch, "E51.12.5", {"start": v(12.4, 8.15) * mm, "end": v(12.78, 8.17) * mm});
            skLineSegment(sketch, "E51.12.6", {"start": v(12.53, 6.82) * mm, "end": v(12.7, 7.07) * mm});
            skLineSegment(sketch, "E51.12.7", {"start": v(13.26, 8.04) * mm, "end": v(13.44, 8.44) * mm});
            skLineSegment(sketch, "E51.12.8", {"start": v(12.35, 6.6) * mm, "end": v(12.53, 6.82) * mm});
            skLineSegment(sketch, "E51.12.9", {"start": v(13.18, 8.17) * mm, "end": v(13.62, 8.15) * mm});
            skLineSegment(sketch, "E51.12.10", {"start": v(13.08, 7.68) * mm, "end": v(13.26, 8.04) * mm});
            skLineSegment(sketch, "E51.12.11", {"start": v(11.76, 8.07) * mm, "end": v(12.07, 8.11) * mm});
            skLineSegment(sketch, "E51.12.12", {"start": v(12.78, 8.17) * mm, "end": v(13.18, 8.17) * mm});
            skLineSegment(sketch, "E51.12.13", {"start": v(11.91, 6.15) * mm, "end": v(12.04, 6.27) * mm});
            skLineSegment(sketch, "E51.12.14", {"start": v(12.04, 6.27) * mm, "end": v(12.2, 6.42) * mm});
            skLineSegment(sketch, "E51.12.15", {"start": v(12.2, 6.42) * mm, "end": v(12.35, 6.6) * mm});
            skLineSegment(sketch, "E51.12.16", {"start": v(11.25, 7.95) * mm, "end": v(11.49, 8) * mm});
            skLineSegment(sketch, "E51.12.17", {"start": v(11.05, 7.89) * mm, "end": v(11.25, 7.95) * mm});
            skLineSegment(sketch, "E51.12.18", {"start": v(11.49, 8) * mm, "end": v(11.76, 8.07) * mm});
            skLineSegment(sketch, "E51.12.19", {"start": v(11.8, 6.05) * mm, "end": v(11.91, 6.15) * mm});
            skLineSegment(sketch, "E51.12.20", {"start": v(11.7, 5.98) * mm, "end": v(11.8, 6.05) * mm});
            skLineSegment(sketch, "E51.12.21", {"start": v(10.88, 7.82) * mm, "end": v(11.05, 7.89) * mm});
            skLineSegment(sketch, "E51.12.22", {"start": v(10.75, 7.77) * mm, "end": v(10.88, 7.82) * mm});
            skLineSegment(sketch, "E51.12.23", {"start": v(10.58, 7.68) * mm, "end": v(10.65, 7.72) * mm});
            skLineSegment(sketch, "E51.12.24", {"start": v(11.59, 5.9) * mm, "end": v(11.6, 5.91) * mm});
            skLineSegment(sketch, "E51.12.25", {"start": v(11.6, 5.91) * mm, "end": v(11.64, 5.94) * mm});
            skLineSegment(sketch, "E51.12.26", {"start": v(10.65, 7.72) * mm, "end": v(10.75, 7.77) * mm});
            skLineSegment(sketch, "E51.12.27", {"start": v(11.64, 5.94) * mm, "end": v(11.7, 5.98) * mm});
            skLineSegment(sketch, "E51.12.28", {"start": v(10.53, 7.65) * mm, "end": v(10.58, 7.68) * mm});
            skLineSegment(sketch, "E51.12.29", {"start": v(10.52, 7.64) * mm, "end": v(10.53, 7.65) * mm});
            skLineSegment(sketch, "E51.13.0", {"start": v(7.64, 10.52) * mm, "end": v(8.25, 11.36) * mm});
            skLineSegment(sketch, "E51.13.1", {"start": v(9.99, 10.98) * mm, "end": v(10.07, 11.34) * mm});
            skLineSegment(sketch, "E51.13.2", {"start": v(9.2, 9.2) * mm, "end": v(9.93, 9.93) * mm});
            skLineSegment(sketch, "E51.13.3", {"start": v(9.9, 10.65) * mm, "end": v(9.99, 10.98) * mm});
            skLineSegment(sketch, "E51.13.4", {"start": v(8.97, 11.44) * mm, "end": v(9.28, 11.58) * mm});
            skLineSegment(sketch, "E51.13.5", {"start": v(9.28, 11.58) * mm, "end": v(9.63, 11.72) * mm});
            skLineSegment(sketch, "E51.13.6", {"start": v(9.8, 10.35) * mm, "end": v(9.9, 10.65) * mm});
            skLineSegment(sketch, "E51.13.7", {"start": v(10.13, 11.74) * mm, "end": v(10.18, 12.18) * mm});
            skLineSegment(sketch, "E51.13.8", {"start": v(9.7, 10.1) * mm, "end": v(9.8, 10.35) * mm});
            skLineSegment(sketch, "E51.13.9", {"start": v(10.01, 11.84) * mm, "end": v(10.44, 11.96) * mm});
            skLineSegment(sketch, "E51.13.10", {"start": v(10.07, 11.34) * mm, "end": v(10.13, 11.74) * mm});
            skLineSegment(sketch, "E51.13.11", {"start": v(8.7, 11.3) * mm, "end": v(8.97, 11.44) * mm});
            skLineSegment(sketch, "E51.13.12", {"start": v(9.63, 11.72) * mm, "end": v(10.01, 11.84) * mm});
            skLineSegment(sketch, "E51.13.13", {"start": v(9.43, 9.53) * mm, "end": v(9.52, 9.68) * mm});
            skLineSegment(sketch, "E51.13.14", {"start": v(9.52, 9.68) * mm, "end": v(9.61, 9.87) * mm});
            skLineSegment(sketch, "E51.13.15", {"start": v(9.61, 9.87) * mm, "end": v(9.7, 10.1) * mm});
            skLineSegment(sketch, "E51.13.16", {"start": v(8.25, 11.04) * mm, "end": v(8.45, 11.17) * mm});
            skLineSegment(sketch, "E51.13.17", {"start": v(8.07, 10.92) * mm, "end": v(8.25, 11.04) * mm});
            skLineSegment(sketch, "E51.13.18", {"start": v(8.45, 11.17) * mm, "end": v(8.7, 11.3) * mm});
            skLineSegment(sketch, "E51.13.19", {"start": v(9.35, 9.4) * mm, "end": v(9.43, 9.53) * mm});
            skLineSegment(sketch, "E51.13.20", {"start": v(9.29, 9.3) * mm, "end": v(9.35, 9.4) * mm});
            skLineSegment(sketch, "E51.13.21", {"start": v(7.93, 10.8) * mm, "end": v(8.07, 10.92) * mm});
            skLineSegment(sketch, "E51.13.22", {"start": v(7.82, 10.7) * mm, "end": v(7.93, 10.8) * mm});
            skLineSegment(sketch, "E51.13.23", {"start": v(7.69, 10.57) * mm, "end": v(7.74, 10.63) * mm});
            skLineSegment(sketch, "E51.13.24", {"start": v(9.2, 9.2) * mm, "end": v(9.2, 9.2) * mm});
            skLineSegment(sketch, "E51.13.25", {"start": v(9.2, 9.2) * mm, "end": v(9.24, 9.24) * mm});
            skLineSegment(sketch, "E51.13.26", {"start": v(7.74, 10.63) * mm, "end": v(7.82, 10.7) * mm});
            skLineSegment(sketch, "E51.13.27", {"start": v(9.24, 9.24) * mm, "end": v(9.29, 9.3) * mm});
            skLineSegment(sketch, "E51.13.28", {"start": v(7.65, 10.53) * mm, "end": v(7.69, 10.57) * mm});
            skLineSegment(sketch, "E51.13.29", {"start": v(7.64, 10.52) * mm, "end": v(7.65, 10.53) * mm});
            skLineSegment(sketch, "E51.14.0", {"start": v(4.02, 12.37) * mm, "end": v(4.34, 13.35) * mm});
            skLineSegment(sketch, "E51.14.1", {"start": v(6.1, 13.53) * mm, "end": v(6.07, 13.9) * mm});
            skLineSegment(sketch, "E51.14.2", {"start": v(5.9, 11.59) * mm, "end": v(6.37, 12.5) * mm});
            skLineSegment(sketch, "E51.14.3", {"start": v(6.13, 13.19) * mm, "end": v(6.1, 13.53) * mm});
            skLineSegment(sketch, "E51.14.4", {"start": v(5, 13.65) * mm, "end": v(5.25, 13.88) * mm});
            skLineSegment(sketch, "E51.14.5", {"start": v(5.25, 13.88) * mm, "end": v(5.54, 14.12) * mm});
            skLineSegment(sketch, "E51.14.6", {"start": v(6.13, 12.88) * mm, "end": v(6.13, 13.19) * mm});
            skLineSegment(sketch, "E51.14.7", {"start": v(6, 14.3) * mm, "end": v(5.92, 14.73) * mm});
            skLineSegment(sketch, "E51.14.8", {"start": v(6.11, 12.6) * mm, "end": v(6.13, 12.88) * mm});
            skLineSegment(sketch, "E51.14.9", {"start": v(5.86, 14.36) * mm, "end": v(6.23, 14.6) * mm});
            skLineSegment(sketch, "E51.14.10", {"start": v(6.07, 13.9) * mm, "end": v(6, 14.3) * mm});
            skLineSegment(sketch, "E51.14.11", {"start": v(4.77, 13.44) * mm, "end": v(5, 13.65) * mm});
            skLineSegment(sketch, "E51.14.12", {"start": v(5.54, 14.12) * mm, "end": v(5.86, 14.36) * mm});
            skLineSegment(sketch, "E51.14.13", {"start": v(6.03, 11.97) * mm, "end": v(6.06, 12.15) * mm});
            skLineSegment(sketch, "E51.14.14", {"start": v(6.06, 12.15) * mm, "end": v(6.1, 12.36) * mm});
            skLineSegment(sketch, "E51.14.15", {"start": v(6.1, 12.36) * mm, "end": v(6.11, 12.6) * mm});
            skLineSegment(sketch, "E51.14.16", {"start": v(4.43, 13.05) * mm, "end": v(4.59, 13.23) * mm});
            skLineSegment(sketch, "E51.14.17", {"start": v(4.3, 12.88) * mm, "end": v(4.43, 13.05) * mm});
            skLineSegment(sketch, "E51.14.18", {"start": v(4.59, 13.23) * mm, "end": v(4.77, 13.44) * mm});
            skLineSegment(sketch, "E51.14.19", {"start": v(5.99, 11.83) * mm, "end": v(6.03, 11.97) * mm});
            skLineSegment(sketch, "E51.14.20", {"start": v(5.96, 11.72) * mm, "end": v(5.99, 11.83) * mm});
            skLineSegment(sketch, "E51.14.21", {"start": v(4.2, 12.73) * mm, "end": v(4.3, 12.88) * mm});
            skLineSegment(sketch, "E51.14.22", {"start": v(4.13, 12.6) * mm, "end": v(4.2, 12.73) * mm});
            skLineSegment(sketch, "E51.14.23", {"start": v(4.04, 12.43) * mm, "end": v(4.08, 12.5) * mm});
            skLineSegment(sketch, "E51.14.24", {"start": v(5.9, 11.59) * mm, "end": v(5.91, 11.6) * mm});
            skLineSegment(sketch, "E51.14.25", {"start": v(5.91, 11.6) * mm, "end": v(5.93, 11.65) * mm});
            skLineSegment(sketch, "E51.14.26", {"start": v(4.08, 12.5) * mm, "end": v(4.13, 12.6) * mm});
            skLineSegment(sketch, "E51.14.27", {"start": v(5.93, 11.65) * mm, "end": v(5.96, 11.72) * mm});
            skLineSegment(sketch, "E51.14.28", {"start": v(4.02, 12.38) * mm, "end": v(4.04, 12.43) * mm});
            skLineSegment(sketch, "E51.14.29", {"start": v(4.02, 12.37) * mm, "end": v(4.02, 12.38) * mm});
            skLineSegment(sketch, "E51.15.0", {"start": v(0, 13) * mm, "end": v(0, 14.04) * mm});
            skLineSegment(sketch, "E51.15.1", {"start": v(1.63, 14.75) * mm, "end": v(1.48, 15.1) * mm});
            skLineSegment(sketch, "E51.15.2", {"start": v(2.03, 12.84) * mm, "end": v(2.2, 13.87) * mm});
            skLineSegment(sketch, "E51.15.3", {"start": v(1.75, 14.43) * mm, "end": v(1.63, 14.75) * mm});
            skLineSegment(sketch, "E51.15.4", {"start": v(0.53, 14.53) * mm, "end": v(0.7, 14.82) * mm});
            skLineSegment(sketch, "E51.15.5", {"start": v(0.7, 14.82) * mm, "end": v(0.9, 15.14) * mm});
            skLineSegment(sketch, "E51.15.6", {"start": v(1.85, 14.14) * mm, "end": v(1.75, 14.43) * mm});
            skLineSegment(sketch, "E51.15.7", {"start": v(1.3, 15.46) * mm, "end": v(1.08, 15.84) * mm});
            skLineSegment(sketch, "E51.15.8", {"start": v(1.92, 13.87) * mm, "end": v(1.85, 14.14) * mm});
            skLineSegment(sketch, "E51.15.9", {"start": v(1.14, 15.47) * mm, "end": v(1.42, 15.81) * mm});
            skLineSegment(sketch, "E51.15.10", {"start": v(1.48, 15.1) * mm, "end": v(1.3, 15.46) * mm});
            skLineSegment(sketch, "E51.15.11", {"start": v(0.39, 14.25) * mm, "end": v(0.53, 14.53) * mm});
            skLineSegment(sketch, "E51.15.12", {"start": v(0.9, 15.14) * mm, "end": v(1.14, 15.47) * mm});
            skLineSegment(sketch, "E51.15.13", {"start": v(2.03, 13.25) * mm, "end": v(2, 13.43) * mm});
            skLineSegment(sketch, "E51.15.14", {"start": v(2, 13.43) * mm, "end": v(1.97, 13.64) * mm});
            skLineSegment(sketch, "E51.15.15", {"start": v(1.97, 13.64) * mm, "end": v(1.92, 13.87) * mm});
            skLineSegment(sketch, "E51.15.16", {"start": v(0.18, 13.78) * mm, "end": v(0.27, 14) * mm});
            skLineSegment(sketch, "E51.15.17", {"start": v(0.12, 13.58) * mm, "end": v(0.18, 13.78) * mm});
            skLineSegment(sketch, "E51.15.18", {"start": v(0.27, 14) * mm, "end": v(0.39, 14.25) * mm});
            skLineSegment(sketch, "E51.15.19", {"start": v(2.04, 13.1) * mm, "end": v(2.03, 13.25) * mm});
            skLineSegment(sketch, "E51.15.20", {"start": v(2.04, 12.99) * mm, "end": v(2.04, 13.1) * mm});
            skLineSegment(sketch, "E51.15.21", {"start": v(0.07, 13.4) * mm, "end": v(0.12, 13.58) * mm});
            skLineSegment(sketch, "E51.15.22", {"start": v(0.03, 13.26) * mm, "end": v(0.07, 13.4) * mm});
            skLineSegment(sketch, "E51.15.23", {"start": v(0, 13.07) * mm, "end": v(0.01, 13.15) * mm});
            skLineSegment(sketch, "E51.15.24", {"start": v(2.03, 12.84) * mm, "end": v(2.04, 12.86) * mm});
            skLineSegment(sketch, "E51.15.25", {"start": v(2.04, 12.86) * mm, "end": v(2.04, 12.9) * mm});
            skLineSegment(sketch, "E51.15.26", {"start": v(0.01, 13.15) * mm, "end": v(0.03, 13.26) * mm});
            skLineSegment(sketch, "E51.15.27", {"start": v(2.04, 12.9) * mm, "end": v(2.04, 12.99) * mm});
            skLineSegment(sketch, "E51.15.28", {"start": v(0, 13.02) * mm, "end": v(0, 13.07) * mm});
            skLineSegment(sketch, "E51.15.29", {"start": v(0, 13) * mm, "end": v(0, 13.02) * mm});
            skLineSegment(sketch, "E51.16.0", {"start": v(-4.02, 12.37) * mm, "end": v(-4.34, 13.35) * mm});
            skLineSegment(sketch, "E51.16.1", {"start": v(-3.01, 14.53) * mm, "end": v(-3.26, 14.81) * mm});
            skLineSegment(sketch, "E51.16.2", {"start": v(-2.03, 12.84) * mm, "end": v(-2.2, 13.87) * mm});
            skLineSegment(sketch, "E51.16.3", {"start": v(-2.8, 14.27) * mm, "end": v(-3.01, 14.53) * mm});
            skLineSegment(sketch, "E51.16.4", {"start": v(-3.99, 13.98) * mm, "end": v(-3.92, 14.32) * mm});
            skLineSegment(sketch, "E51.16.5", {"start": v(-3.92, 14.32) * mm, "end": v(-3.82, 14.68) * mm});
            skLineSegment(sketch, "E51.16.6", {"start": v(-2.61, 14.02) * mm, "end": v(-2.8, 14.27) * mm});
            skLineSegment(sketch, "E51.16.7", {"start": v(-3.55, 15.1) * mm, "end": v(-3.87, 15.4) * mm});
            skLineSegment(sketch, "E51.16.8", {"start": v(-2.46, 13.79) * mm, "end": v(-2.61, 14.02) * mm});
            skLineSegment(sketch, "E51.16.9", {"start": v(-3.7, 15.06) * mm, "end": v(-3.54, 15.47) * mm});
            skLineSegment(sketch, "E51.16.10", {"start": v(-3.26, 14.81) * mm, "end": v(-3.55, 15.1) * mm});
            skLineSegment(sketch, "E51.16.11", {"start": v(-4.04, 13.68) * mm, "end": v(-3.99, 13.98) * mm});
            skLineSegment(sketch, "E51.16.12", {"start": v(-3.82, 14.68) * mm, "end": v(-3.7, 15.06) * mm});
            skLineSegment(sketch, "E51.16.13", {"start": v(-2.16, 13.23) * mm, "end": v(-2.24, 13.4) * mm});
            skLineSegment(sketch, "E51.16.14", {"start": v(-2.24, 13.4) * mm, "end": v(-2.34, 13.58) * mm});
            skLineSegment(sketch, "E51.16.15", {"start": v(-2.34, 13.58) * mm, "end": v(-2.46, 13.79) * mm});
            skLineSegment(sketch, "E51.16.16", {"start": v(-4.08, 13.16) * mm, "end": v(-4.07, 13.4) * mm});
            skLineSegment(sketch, "E51.16.17", {"start": v(-4.08, 12.95) * mm, "end": v(-4.08, 13.16) * mm});
            skLineSegment(sketch, "E51.16.18", {"start": v(-4.07, 13.4) * mm, "end": v(-4.04, 13.68) * mm});
            skLineSegment(sketch, "E51.16.19", {"start": v(-2.1, 13.1) * mm, "end": v(-2.16, 13.23) * mm});
            skLineSegment(sketch, "E51.16.20", {"start": v(-2.07, 12.99) * mm, "end": v(-2.1, 13.1) * mm});
            skLineSegment(sketch, "E51.16.21", {"start": v(-4.08, 12.77) * mm, "end": v(-4.08, 12.95) * mm});
            skLineSegment(sketch, "E51.16.22", {"start": v(-4.07, 12.62) * mm, "end": v(-4.08, 12.77) * mm});
            skLineSegment(sketch, "E51.16.23", {"start": v(-4.03, 12.43) * mm, "end": v(-4.05, 12.51) * mm});
            skLineSegment(sketch, "E51.16.24", {"start": v(-2.03, 12.84) * mm, "end": v(-2.04, 12.86) * mm});
            skLineSegment(sketch, "E51.16.25", {"start": v(-2.04, 12.86) * mm, "end": v(-2.05, 12.9) * mm});
            skLineSegment(sketch, "E51.16.26", {"start": v(-4.05, 12.51) * mm, "end": v(-4.07, 12.62) * mm});
            skLineSegment(sketch, "E51.16.27", {"start": v(-2.05, 12.9) * mm, "end": v(-2.07, 12.99) * mm});
            skLineSegment(sketch, "E51.16.28", {"start": v(-4.02, 12.38) * mm, "end": v(-4.03, 12.43) * mm});
            skLineSegment(sketch, "E51.16.29", {"start": v(-4.02, 12.37) * mm, "end": v(-4.02, 12.38) * mm});
            skLineSegment(sketch, "E51.17.0", {"start": v(-7.64, 10.52) * mm, "end": v(-8.25, 11.36) * mm});
            skLineSegment(sketch, "E51.17.1", {"start": v(-7.35, 12.9) * mm, "end": v(-7.68, 13.08) * mm});
            skLineSegment(sketch, "E51.17.2", {"start": v(-5.9, 11.59) * mm, "end": v(-6.37, 12.5) * mm});
            skLineSegment(sketch, "E51.17.3", {"start": v(-7.07, 12.7) * mm, "end": v(-7.35, 12.9) * mm});
            skLineSegment(sketch, "E51.17.4", {"start": v(-8.11, 12.07) * mm, "end": v(-8.15, 12.4) * mm});
            skLineSegment(sketch, "E51.17.5", {"start": v(-8.15, 12.4) * mm, "end": v(-8.17, 12.78) * mm});
            skLineSegment(sketch, "E51.17.6", {"start": v(-6.82, 12.53) * mm, "end": v(-7.07, 12.7) * mm});
            skLineSegment(sketch, "E51.17.7", {"start": v(-8.04, 13.26) * mm, "end": v(-8.44, 13.44) * mm});
            skLineSegment(sketch, "E51.17.8", {"start": v(-6.6, 12.35) * mm, "end": v(-6.82, 12.53) * mm});
            skLineSegment(sketch, "E51.17.9", {"start": v(-8.17, 13.18) * mm, "end": v(-8.15, 13.62) * mm});
            skLineSegment(sketch, "E51.17.10", {"start": v(-7.68, 13.08) * mm, "end": v(-8.04, 13.26) * mm});
            skLineSegment(sketch, "E51.17.11", {"start": v(-8.07, 11.76) * mm, "end": v(-8.11, 12.07) * mm});
            skLineSegment(sketch, "E51.17.12", {"start": v(-8.17, 12.78) * mm, "end": v(-8.17, 13.18) * mm});
            skLineSegment(sketch, "E51.17.13", {"start": v(-6.15, 11.91) * mm, "end": v(-6.27, 12.04) * mm});
            skLineSegment(sketch, "E51.17.14", {"start": v(-6.27, 12.04) * mm, "end": v(-6.42, 12.2) * mm});
            skLineSegment(sketch, "E51.17.15", {"start": v(-6.42, 12.2) * mm, "end": v(-6.6, 12.35) * mm});
            skLineSegment(sketch, "E51.17.16", {"start": v(-7.95, 11.25) * mm, "end": v(-8, 11.49) * mm});
            skLineSegment(sketch, "E51.17.17", {"start": v(-7.89, 11.05) * mm, "end": v(-7.95, 11.25) * mm});
            skLineSegment(sketch, "E51.17.18", {"start": v(-8, 11.49) * mm, "end": v(-8.07, 11.76) * mm});
            skLineSegment(sketch, "E51.17.19", {"start": v(-6.05, 11.8) * mm, "end": v(-6.15, 11.91) * mm});
            skLineSegment(sketch, "E51.17.20", {"start": v(-5.98, 11.7) * mm, "end": v(-6.05, 11.8) * mm});
            skLineSegment(sketch, "E51.17.21", {"start": v(-7.82, 10.88) * mm, "end": v(-7.89, 11.05) * mm});
            skLineSegment(sketch, "E51.17.22", {"start": v(-7.77, 10.75) * mm, "end": v(-7.82, 10.88) * mm});
            skLineSegment(sketch, "E51.17.23", {"start": v(-7.68, 10.58) * mm, "end": v(-7.72, 10.65) * mm});
            skLineSegment(sketch, "E51.17.24", {"start": v(-5.9, 11.59) * mm, "end": v(-5.91, 11.6) * mm});
            skLineSegment(sketch, "E51.17.25", {"start": v(-5.91, 11.6) * mm, "end": v(-5.94, 11.64) * mm});
            skLineSegment(sketch, "E51.17.26", {"start": v(-7.72, 10.65) * mm, "end": v(-7.77, 10.75) * mm});
            skLineSegment(sketch, "E51.17.27", {"start": v(-5.94, 11.64) * mm, "end": v(-5.98, 11.7) * mm});
            skLineSegment(sketch, "E51.17.28", {"start": v(-7.65, 10.53) * mm, "end": v(-7.68, 10.58) * mm});
            skLineSegment(sketch, "E51.17.29", {"start": v(-7.64, 10.52) * mm, "end": v(-7.65, 10.53) * mm});
            skLineSegment(sketch, "E51.18.0", {"start": v(-10.52, 7.64) * mm, "end": v(-11.36, 8.25) * mm});
            skLineSegment(sketch, "E51.18.1", {"start": v(-10.98, 9.99) * mm, "end": v(-11.34, 10.07) * mm});
            skLineSegment(sketch, "E51.18.2", {"start": v(-9.2, 9.2) * mm, "end": v(-9.93, 9.93) * mm});
            skLineSegment(sketch, "E51.18.3", {"start": v(-10.65, 9.9) * mm, "end": v(-10.98, 9.99) * mm});
            skLineSegment(sketch, "E51.18.4", {"start": v(-11.44, 8.97) * mm, "end": v(-11.58, 9.28) * mm});
            skLineSegment(sketch, "E51.18.5", {"start": v(-11.58, 9.28) * mm, "end": v(-11.72, 9.63) * mm});
            skLineSegment(sketch, "E51.18.6", {"start": v(-10.35, 9.8) * mm, "end": v(-10.65, 9.9) * mm});
            skLineSegment(sketch, "E51.18.7", {"start": v(-11.74, 10.13) * mm, "end": v(-12.18, 10.18) * mm});
            skLineSegment(sketch, "E51.18.8", {"start": v(-10.1, 9.7) * mm, "end": v(-10.35, 9.8) * mm});
            skLineSegment(sketch, "E51.18.9", {"start": v(-11.84, 10.01) * mm, "end": v(-11.96, 10.44) * mm});
            skLineSegment(sketch, "E51.18.10", {"start": v(-11.34, 10.07) * mm, "end": v(-11.74, 10.13) * mm});
            skLineSegment(sketch, "E51.18.11", {"start": v(-11.3, 8.7) * mm, "end": v(-11.44, 8.97) * mm});
            skLineSegment(sketch, "E51.18.12", {"start": v(-11.72, 9.63) * mm, "end": v(-11.84, 10.01) * mm});
            skLineSegment(sketch, "E51.18.13", {"start": v(-9.53, 9.43) * mm, "end": v(-9.68, 9.52) * mm});
            skLineSegment(sketch, "E51.18.14", {"start": v(-9.68, 9.52) * mm, "end": v(-9.87, 9.61) * mm});
            skLineSegment(sketch, "E51.18.15", {"start": v(-9.87, 9.61) * mm, "end": v(-10.1, 9.7) * mm});
            skLineSegment(sketch, "E51.18.16", {"start": v(-11.04, 8.25) * mm, "end": v(-11.17, 8.45) * mm});
            skLineSegment(sketch, "E51.18.17", {"start": v(-10.92, 8.07) * mm, "end": v(-11.04, 8.25) * mm});
            skLineSegment(sketch, "E51.18.18", {"start": v(-11.17, 8.45) * mm, "end": v(-11.3, 8.7) * mm});
            skLineSegment(sketch, "E51.18.19", {"start": v(-9.4, 9.35) * mm, "end": v(-9.53, 9.43) * mm});
            skLineSegment(sketch, "E51.18.20", {"start": v(-9.3, 9.29) * mm, "end": v(-9.4, 9.35) * mm});
            skLineSegment(sketch, "E51.18.21", {"start": v(-10.8, 7.93) * mm, "end": v(-10.92, 8.07) * mm});
            skLineSegment(sketch, "E51.18.22", {"start": v(-10.7, 7.82) * mm, "end": v(-10.8, 7.93) * mm});
            skLineSegment(sketch, "E51.18.23", {"start": v(-10.57, 7.69) * mm, "end": v(-10.63, 7.74) * mm});
            skLineSegment(sketch, "E51.18.24", {"start": v(-9.2, 9.2) * mm, "end": v(-9.2, 9.2) * mm});
            skLineSegment(sketch, "E51.18.25", {"start": v(-9.2, 9.2) * mm, "end": v(-9.24, 9.24) * mm});
            skLineSegment(sketch, "E51.18.26", {"start": v(-10.63, 7.74) * mm, "end": v(-10.7, 7.82) * mm});
            skLineSegment(sketch, "E51.18.27", {"start": v(-9.24, 9.24) * mm, "end": v(-9.3, 9.29) * mm});
            skLineSegment(sketch, "E51.18.28", {"start": v(-10.53, 7.65) * mm, "end": v(-10.57, 7.69) * mm});
            skLineSegment(sketch, "E51.18.29", {"start": v(-10.52, 7.64) * mm, "end": v(-10.53, 7.65) * mm});
            skLineSegment(sketch, "E51.19.0", {"start": v(-12.37, 4.02) * mm, "end": v(-13.35, 4.34) * mm});
            skLineSegment(sketch, "E51.19.1", {"start": v(-13.53, 6.1) * mm, "end": v(-13.9, 6.07) * mm});
            skLineSegment(sketch, "E51.19.2", {"start": v(-11.59, 5.9) * mm, "end": v(-12.5, 6.37) * mm});
            skLineSegment(sketch, "E51.19.3", {"start": v(-13.19, 6.13) * mm, "end": v(-13.53, 6.1) * mm});
            skLineSegment(sketch, "E51.19.4", {"start": v(-13.65, 5) * mm, "end": v(-13.88, 5.25) * mm});
            skLineSegment(sketch, "E51.19.5", {"start": v(-13.88, 5.25) * mm, "end": v(-14.12, 5.54) * mm});
            skLineSegment(sketch, "E51.19.6", {"start": v(-12.88, 6.13) * mm, "end": v(-13.19, 6.13) * mm});
            skLineSegment(sketch, "E51.19.7", {"start": v(-14.3, 6) * mm, "end": v(-14.73, 5.92) * mm});
            skLineSegment(sketch, "E51.19.8", {"start": v(-12.6, 6.11) * mm, "end": v(-12.88, 6.13) * mm});
            skLineSegment(sketch, "E51.19.9", {"start": v(-14.36, 5.86) * mm, "end": v(-14.6, 6.23) * mm});
            skLineSegment(sketch, "E51.19.10", {"start": v(-13.9, 6.07) * mm, "end": v(-14.3, 6) * mm});
            skLineSegment(sketch, "E51.19.11", {"start": v(-13.44, 4.77) * mm, "end": v(-13.65, 5) * mm});
            skLineSegment(sketch, "E51.19.12", {"start": v(-14.12, 5.54) * mm, "end": v(-14.36, 5.86) * mm});
            skLineSegment(sketch, "E51.19.13", {"start": v(-11.97, 6.03) * mm, "end": v(-12.15, 6.06) * mm});
            skLineSegment(sketch, "E51.19.14", {"start": v(-12.15, 6.06) * mm, "end": v(-12.36, 6.1) * mm});
            skLineSegment(sketch, "E51.19.15", {"start": v(-12.36, 6.1) * mm, "end": v(-12.6, 6.11) * mm});
            skLineSegment(sketch, "E51.19.16", {"start": v(-13.05, 4.43) * mm, "end": v(-13.23, 4.59) * mm});
            skLineSegment(sketch, "E51.19.17", {"start": v(-12.88, 4.3) * mm, "end": v(-13.05, 4.43) * mm});
            skLineSegment(sketch, "E51.19.18", {"start": v(-13.23, 4.59) * mm, "end": v(-13.44, 4.77) * mm});
            skLineSegment(sketch, "E51.19.19", {"start": v(-11.83, 5.99) * mm, "end": v(-11.97, 6.03) * mm});
            skLineSegment(sketch, "E51.19.20", {"start": v(-11.72, 5.96) * mm, "end": v(-11.83, 5.99) * mm});
            skLineSegment(sketch, "E51.19.21", {"start": v(-12.73, 4.2) * mm, "end": v(-12.88, 4.3) * mm});
            skLineSegment(sketch, "E51.19.22", {"start": v(-12.6, 4.13) * mm, "end": v(-12.73, 4.2) * mm});
            skLineSegment(sketch, "E51.19.23", {"start": v(-12.43, 4.04) * mm, "end": v(-12.5, 4.08) * mm});
            skLineSegment(sketch, "E51.19.24", {"start": v(-11.59, 5.9) * mm, "end": v(-11.6, 5.91) * mm});
            skLineSegment(sketch, "E51.19.25", {"start": v(-11.6, 5.91) * mm, "end": v(-11.65, 5.93) * mm});
            skLineSegment(sketch, "E51.19.26", {"start": v(-12.5, 4.08) * mm, "end": v(-12.6, 4.13) * mm});
            skLineSegment(sketch, "E51.19.27", {"start": v(-11.65, 5.93) * mm, "end": v(-11.72, 5.96) * mm});
            skLineSegment(sketch, "E51.19.28", {"start": v(-12.38, 4.02) * mm, "end": v(-12.43, 4.04) * mm});
            skLineSegment(sketch, "E51.19.29", {"start": v(-12.37, 4.02) * mm, "end": v(-12.38, 4.02) * mm});
            skSolve(sketch);
        }
        {
            var Q0;
            {var subQ0=sQuery(id+"F1.wireOp",EDGE,"E0");var subQ27=makeQuery(id+"F1.imprint","INTERSECT",VERTEX,{"derivedFrom":[subQ0,sQuery(id+"F1.wireOp",EDGE,"E51.10.0")]});Q0=makeQuery(id+"F1.imprint","IMPRINT",FACE,{"disambiguationData":[TD([[makeQuery(id+"F1.imprint","IMPRINT",EDGE,{"disambiguationData":[TD([[subQ27,-1.0]])],"derivedFrom":subQ0}),1.0]])]});}
            var Q1;
            {var subQ0=sQuery(id+"F1.wireOp",EDGE,"E51.1.0");Q1=makeQuery(id+"F1.imprint","IMPRINT",FACE,{"disambiguationData":[TD([[makeQuery(id+"F1.imprint","IMPRINT",EDGE,{"derivedFrom":subQ0}),-1.0]])]});}
            var Q2;
            {var subQ7=sQuery(id+"F1.wireOp",EDGE,"E51.2.0");Q2=makeQuery(id+"F1.imprint","IMPRINT",FACE,{"disambiguationData":[TD([[makeQuery(id+"F1.imprint","IMPRINT",EDGE,{"derivedFrom":subQ7}),-1.0]])]});}
            var Q3;
            {var subQ8=sQuery(id+"F1.wireOp",EDGE,"E51.3.0");Q3=makeQuery(id+"F1.imprint","IMPRINT",FACE,{"disambiguationData":[TD([[makeQuery(id+"F1.imprint","IMPRINT",EDGE,{"derivedFrom":subQ8}),-1.0]])]});}
            var Q4;
            {var subQ2=sQuery(id+"F1.wireOp",EDGE,"E51.4.0");Q4=makeQuery(id+"F1.imprint","IMPRINT",FACE,{"disambiguationData":[TD([[makeQuery(id+"F1.imprint","IMPRINT",EDGE,{"derivedFrom":subQ2}),-1.0]])]});}
            var Q5;
            {var subQ8=sQuery(id+"F1.wireOp",EDGE,"E51.5.0");Q5=makeQuery(id+"F1.imprint","IMPRINT",FACE,{"disambiguationData":[TD([[makeQuery(id+"F1.imprint","IMPRINT",EDGE,{"derivedFrom":subQ8}),-1.0]])]});}
            var Q6;
            {var subQ3=sQuery(id+"F1.wireOp",EDGE,"E51.6.0");Q6=makeQuery(id+"F1.imprint","IMPRINT",FACE,{"disambiguationData":[TD([[makeQuery(id+"F1.imprint","IMPRINT",EDGE,{"derivedFrom":subQ3}),-1.0]])]});}
            var Q7;
            {var subQ0=sQuery(id+"F1.wireOp",EDGE,"E51.7.0");Q7=makeQuery(id+"F1.imprint","IMPRINT",FACE,{"disambiguationData":[TD([[makeQuery(id+"F1.imprint","IMPRINT",EDGE,{"derivedFrom":subQ0}),-1.0]])]});}
            var Q8;
            {var subQ5=sQuery(id+"F1.wireOp",EDGE,"E51.8.0");Q8=makeQuery(id+"F1.imprint","IMPRINT",FACE,{"disambiguationData":[TD([[makeQuery(id+"F1.imprint","IMPRINT",EDGE,{"derivedFrom":subQ5}),-1.0]])]});}
            var Q9;
            {var subQ1=sQuery(id+"F1.wireOp",EDGE,"E51.9.0");Q9=makeQuery(id+"F1.imprint","IMPRINT",FACE,{"disambiguationData":[TD([[makeQuery(id+"F1.imprint","IMPRINT",EDGE,{"derivedFrom":subQ1}),-1.0]])]});}
            var Q10;
            {var subQ5=sQuery(id+"F1.wireOp",EDGE,"E51.10.0");Q10=makeQuery(id+"F1.imprint","IMPRINT",FACE,{"disambiguationData":[TD([[makeQuery(id+"F1.imprint","IMPRINT",EDGE,{"derivedFrom":subQ5}),-1.0]])]});}
            var Q11;
            {var subQ8=sQuery(id+"F1.wireOp",EDGE,"E51.11.0");Q11=makeQuery(id+"F1.imprint","IMPRINT",FACE,{"disambiguationData":[TD([[makeQuery(id+"F1.imprint","IMPRINT",EDGE,{"derivedFrom":subQ8}),-1.0]])]});}
            var Q12;
            {var subQ2=sQuery(id+"F1.wireOp",EDGE,"E51.12.0");Q12=makeQuery(id+"F1.imprint","IMPRINT",FACE,{"disambiguationData":[TD([[makeQuery(id+"F1.imprint","IMPRINT",EDGE,{"derivedFrom":subQ2}),-1.0]])]});}
            var Q13;
            {var subQ3=sQuery(id+"F1.wireOp",EDGE,"E51.13.0");Q13=makeQuery(id+"F1.imprint","IMPRINT",FACE,{"disambiguationData":[TD([[makeQuery(id+"F1.imprint","IMPRINT",EDGE,{"derivedFrom":subQ3}),-1.0]])]});}
            var Q14;
            {var subQ0=sQuery(id+"F1.wireOp",EDGE,"E51.14.0");Q14=makeQuery(id+"F1.imprint","IMPRINT",FACE,{"disambiguationData":[TD([[makeQuery(id+"F1.imprint","IMPRINT",EDGE,{"derivedFrom":subQ0}),-1.0]])]});}
            var Q15;
            {var subQ6=sQuery(id+"F1.wireOp",EDGE,"E51.15.0");Q15=makeQuery(id+"F1.imprint","IMPRINT",FACE,{"disambiguationData":[TD([[makeQuery(id+"F1.imprint","IMPRINT",EDGE,{"derivedFrom":subQ6}),-1.0]])]});}
            var Q16;
            {var subQ5=sQuery(id+"F1.wireOp",EDGE,"E51.16.0");Q16=makeQuery(id+"F1.imprint","IMPRINT",FACE,{"disambiguationData":[TD([[makeQuery(id+"F1.imprint","IMPRINT",EDGE,{"derivedFrom":subQ5}),-1.0]])]});}
            var Q17;
            {var subQ7=sQuery(id+"F1.wireOp",EDGE,"E51.17.0");Q17=makeQuery(id+"F1.imprint","IMPRINT",FACE,{"disambiguationData":[TD([[makeQuery(id+"F1.imprint","IMPRINT",EDGE,{"derivedFrom":subQ7}),-1.0]])]});}
            var Q18;
            {var subQ5=sQuery(id+"F1.wireOp",EDGE,"E51.18.0");Q18=makeQuery(id+"F1.imprint","IMPRINT",FACE,{"disambiguationData":[TD([[makeQuery(id+"F1.imprint","IMPRINT",EDGE,{"derivedFrom":subQ5}),-1.0]])]});}
            var Q19;
            {var subQ8=sQuery(id+"F1.wireOp",EDGE,"E51.19.0");Q19=makeQuery(id+"F1.imprint","IMPRINT",FACE,{"disambiguationData":[TD([[makeQuery(id+"F1.imprint","IMPRINT",EDGE,{"derivedFrom":subQ8}),-1.0]])]});}
            var Q20;
            {var subQ8=sQuery(id+"F1.wireOp",EDGE,"E21");Q20=makeQuery(id+"F1.imprint","IMPRINT",FACE,{"disambiguationData":[TD([[makeQuery(id+"F1.imprint","IMPRINT",EDGE,{"derivedFrom":subQ8}),-1.0]])]});}
            extrude(context, id + "F2", {"entities" : qUnion([Q0, Q1, Q2, Q3, Q4, Q5, Q6, Q7, Q8, Q9, Q10, Q11, Q12, Q13, Q14, Q15, Q16, Q17, Q18, Q19, Q20]), "depth" : (getVariable(context, 'GearThickness')) * mm});
        }
    });
